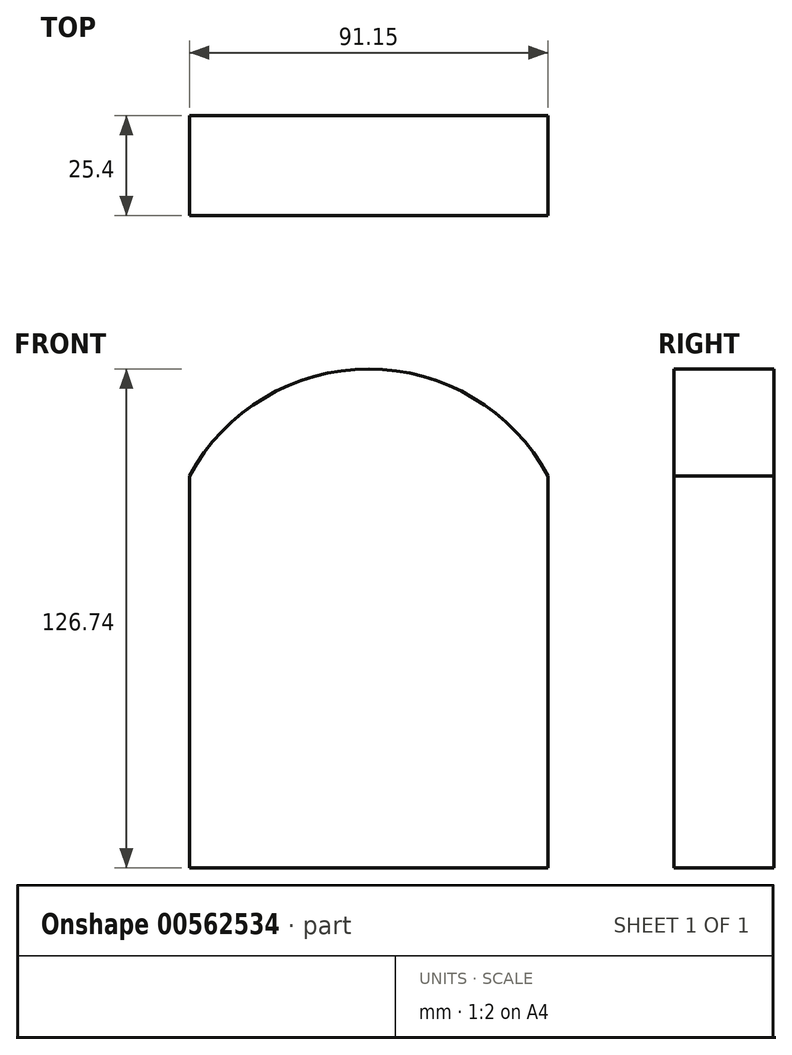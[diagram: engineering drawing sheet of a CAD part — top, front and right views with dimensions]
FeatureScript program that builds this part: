
annotation { "Feature Type Name" : "Feature", "Feature Type Description" : "" }
export const myFeature = defineFeature(function(context is Context, id is Id, definition is map)
    precondition{}
    {
        {
            var Q0;
            Q0=qCreatedBy(makeId("Front.planeOp"),FACE);
            var sketch = newSketch(context, id + "F0", { "sketchPlane" : qUnion([Q0])});
            skLineSegment(sketch, "E0.top", {"start": v(-46.09, -56.2) * mm, "end": v(45.06, -56.2) * mm});
            skLineSegment(sketch, "E0.left", {"start": v(-46.09, 43.4) * mm, "end": v(-46.09, -56.2) * mm});
            skLineSegment(sketch, "E0.right", {"start": v(45.06, 43.4) * mm, "end": v(45.06, -56.2) * mm});
            skLineSegment(sketch, "E1", {"start": v(0, 0) * mm, "end": v(0, 70.54) * mm});
            skArc(sketch, "E2", {"start": v(45.06, 43.4) * mm, "mid": v(-0.51, 70.54) * mm, "end": v(-46.09, 43.4) * mm});
            skLineSegment(sketch, "E3", {"start": v(-76.3, -62.35) * mm, "end": v(75.53, -62.35) * mm});
            skSolve(sketch);
        }
        {
            var Q0;
            Q0=makeQuery(id+"F0.imprint","IMPRINT",FACE,{"disambiguationData":[TD([[makeQuery(id+"F0.imprint","IMPRINT",EDGE,{"derivedFrom":sQuery(id+"F0.wireOp",EDGE,"E0.top")}),1.0]])]});
            extrude(context, id + "F1", {"entities" : qUnion([Q0]), "depth" : 25.4 * mm, "offsetDistance" : 25.4 * mm});
        }
    });
